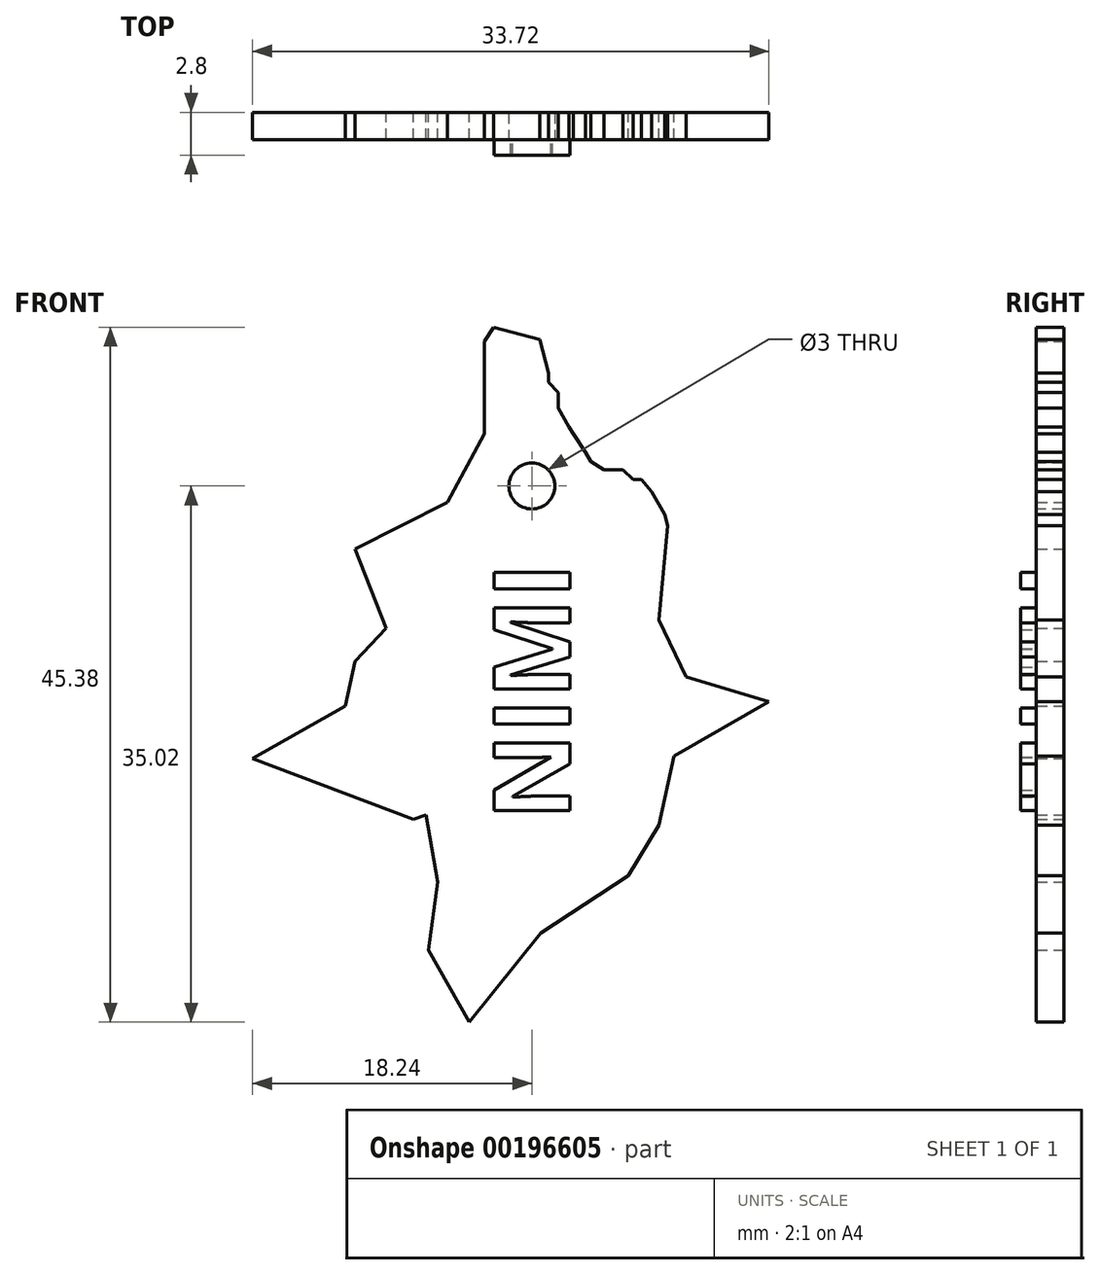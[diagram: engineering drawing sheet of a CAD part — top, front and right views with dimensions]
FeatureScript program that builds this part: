
annotation { "Feature Type Name" : "Feature", "Feature Type Description" : "" }
export const myFeature = defineFeature(function(context is Context, id is Id, definition is map)
    precondition{}
    {
        {
            var Q0;
            Q0=qCreatedBy(makeId("Front.planeOp"),FACE);
            var sketch = newSketch(context, id + "F0", { "sketchPlane" : qUnion([Q0])});
            skLineSegment(sketch, "E0", {"start": v(-3.64, 39.6) * mm, "end": v(1.4, 38.3) * mm});
            skLineSegment(sketch, "E1", {"start": v(1.4, 38.3) * mm, "end": v(2.35, 34.63) * mm});
            skLineSegment(sketch, "E2", {"start": v(2.35, 34.63) * mm, "end": v(2.35, 33.62) * mm});
            skLineSegment(sketch, "E3", {"start": v(2.35, 33.62) * mm, "end": v(3.37, 32.54) * mm});
            skLineSegment(sketch, "E4", {"start": v(3.37, 32.54) * mm, "end": v(3.37, 30.85) * mm});
            skLineSegment(sketch, "E5", {"start": v(3.37, 30.85) * mm, "end": v(4.55, 28.76) * mm});
            skLineSegment(sketch, "E6", {"start": v(4.55, 28.76) * mm, "end": v(5, 28.03) * mm});
            skLineSegment(sketch, "E7", {"start": v(5, 28.03) * mm, "end": v(6.36, 26) * mm});
            skLineSegment(sketch, "E8", {"start": v(6.36, 26) * mm, "end": v(6.92, 25.02) * mm});
            skLineSegment(sketch, "E9", {"start": v(6.92, 25.02) * mm, "end": v(8.34, 24.13) * mm});
            skLineSegment(sketch, "E10", {"start": v(8.34, 24.13) * mm, "end": v(10.43, 24.13) * mm});
            skLineSegment(sketch, "E11", {"start": v(10.43, 24.13) * mm, "end": v(11.56, 23.05) * mm});
            skLineSegment(sketch, "E12", {"start": v(11.56, 23.05) * mm, "end": v(12.46, 23.05) * mm});
            skLineSegment(sketch, "E13", {"start": v(12.46, 23.05) * mm, "end": v(13.56, 21.75) * mm});
            skLineSegment(sketch, "E14", {"start": v(13.56, 21.75) * mm, "end": v(14.32, 20.42) * mm});
            skLineSegment(sketch, "E15", {"start": v(14.32, 20.42) * mm, "end": v(14.98, 19.25) * mm});
            skLineSegment(sketch, "E16", {"start": v(14.98, 19.25) * mm, "end": v(15.3, 18) * mm});
            skLineSegment(sketch, "E17", {"start": v(15.3, 18) * mm, "end": v(14.32, 7.76) * mm});
            skLineSegment(sketch, "E18", {"start": v(14.32, 7.76) * mm, "end": v(17.31, 1.56) * mm});
            skLineSegment(sketch, "E19", {"start": v(17.31, 1.56) * mm, "end": v(26.32, -1.15) * mm});
            skLineSegment(sketch, "E20", {"start": v(26.32, -1.15) * mm, "end": v(15.96, -7.03) * mm});
            skLineSegment(sketch, "E21", {"start": v(15.96, -7.03) * mm, "end": v(14.32, -14.58) * mm});
            skLineSegment(sketch, "E22", {"start": v(14.32, -14.58) * mm, "end": v(11, -20.07) * mm});
            skLineSegment(sketch, "E23", {"start": v(11, -20.07) * mm, "end": v(1.49, -26.31) * mm});
            skLineSegment(sketch, "E24", {"start": v(1.49, -26.31) * mm, "end": v(-6.28, -36.02) * mm});
            skLineSegment(sketch, "E25", {"start": v(-6.28, -36.02) * mm, "end": v(-10.72, -28.18) * mm});
            skLineSegment(sketch, "E26", {"start": v(-10.72, -28.18) * mm, "end": v(-9.75, -20.77) * mm});
            skLineSegment(sketch, "E27", {"start": v(-9.75, -20.77) * mm, "end": v(-11, -13.47) * mm});
            skLineSegment(sketch, "E28", {"start": v(-11, -13.47) * mm, "end": v(-12.4, -13.92) * mm});
            skLineSegment(sketch, "E29", {"start": v(-12.4, -13.92) * mm, "end": v(-29.89, -7.33) * mm});
            skLineSegment(sketch, "E30", {"start": v(-29.89, -7.33) * mm, "end": v(-19.8, -1.6) * mm});
            skLineSegment(sketch, "E31", {"start": v(-19.8, -1.6) * mm, "end": v(-18.74, 3.26) * mm});
            skLineSegment(sketch, "E32", {"start": v(-18.74, 3.26) * mm, "end": v(-15.36, 6.85) * mm});
            skLineSegment(sketch, "E33", {"start": v(-15.36, 6.85) * mm, "end": v(-18.73, 15.49) * mm});
            skLineSegment(sketch, "E34", {"start": v(-18.73, 15.49) * mm, "end": v(-8.7, 20.57) * mm});
            skLineSegment(sketch, "E35", {"start": v(-8.7, 20.57) * mm, "end": v(-4.66, 28.05) * mm});
            skLineSegment(sketch, "E36", {"start": v(-4.66, 28.05) * mm, "end": v(-4.66, 38.08) * mm});
            skLineSegment(sketch, "E37", {"start": v(-4.66, 38.08) * mm, "end": v(-3.64, 39.6) * mm});
            skSolve(sketch);
        }
        {
            var Q0;
            Q0=makeQuery(id+"F0.imprint","IMPRINT",FACE,{"disambiguationData":[TD([[makeQuery(id+"F0.imprint","IMPRINT",EDGE,{"derivedFrom":sQuery(id+"F0.wireOp",EDGE,"E0")}),-1.0]])]});
            extrude(context, id + "F1", {"entities" : qUnion([Q0]), "depth" : 3 * mm});
        }
        {
            var Q0;
            Q0=makeQuery(id+"F1.opExtrude","SWEPT_BODY",BODY,{"disambiguationData":[OSD([sQuery(id+"F0.wireOp",EDGE,"E0"),sQuery(id+"F0.wireOp",EDGE,"E1"),sQuery(id+"F0.wireOp",EDGE,"E2"),sQuery(id+"F0.wireOp",EDGE,"E3"),sQuery(id+"F0.wireOp",EDGE,"E4"),sQuery(id+"F0.wireOp",EDGE,"E5"),sQuery(id+"F0.wireOp",EDGE,"E6"),sQuery(id+"F0.wireOp",EDGE,"E7"),sQuery(id+"F0.wireOp",EDGE,"E8"),sQuery(id+"F0.wireOp",EDGE,"E9"),sQuery(id+"F0.wireOp",EDGE,"E10"),sQuery(id+"F0.wireOp",EDGE,"E11"),sQuery(id+"F0.wireOp",EDGE,"E12"),sQuery(id+"F0.wireOp",EDGE,"E13"),sQuery(id+"F0.wireOp",EDGE,"E14"),sQuery(id+"F0.wireOp",EDGE,"E15"),sQuery(id+"F0.wireOp",EDGE,"E16"),sQuery(id+"F0.wireOp",EDGE,"E17"),sQuery(id+"F0.wireOp",EDGE,"E18"),sQuery(id+"F0.wireOp",EDGE,"E19"),sQuery(id+"F0.wireOp",EDGE,"E20"),sQuery(id+"F0.wireOp",EDGE,"E21"),sQuery(id+"F0.wireOp",EDGE,"E22"),sQuery(id+"F0.wireOp",EDGE,"E23"),sQuery(id+"F0.wireOp",EDGE,"E24"),sQuery(id+"F0.wireOp",EDGE,"E25"),sQuery(id+"F0.wireOp",EDGE,"E26"),sQuery(id+"F0.wireOp",EDGE,"E27"),sQuery(id+"F0.wireOp",EDGE,"E28"),sQuery(id+"F0.wireOp",EDGE,"E29"),sQuery(id+"F0.wireOp",EDGE,"E30"),sQuery(id+"F0.wireOp",EDGE,"E31"),sQuery(id+"F0.wireOp",EDGE,"E32"),sQuery(id+"F0.wireOp",EDGE,"E33"),sQuery(id+"F0.wireOp",EDGE,"E34"),sQuery(id+"F0.wireOp",EDGE,"E35"),sQuery(id+"F0.wireOp",EDGE,"E36"),sQuery(id+"F0.wireOp",EDGE,"E37")])]});
            var Q1;
            Q1=makeQuery(id+"F1.opExtrude","CAP_VERTEX",VERTEX,{"disambiguationData":[OSD([sQuery(id+"F0.wireOp",EDGE,"E24"),sQuery(id+"F0.wireOp",EDGE,"E25")])],"isStart":false});
            transform(context, id + "F2", {"entities" : qUnion([Q0]), "transformType" : TransformType.SCALE_UNIFORMLY, "scale" : 0.6, "scalePoint" : qUnion([Q1]), "makeCopy" : false});
        }
        {
            var Q0;
            Q0=makeQuery(id+"F1.opExtrude","CAP_FACE",FACE,{"disambiguationData":[OSD([sQuery(id+"F0.wireOp",EDGE,"E0"),sQuery(id+"F0.wireOp",EDGE,"E1"),sQuery(id+"F0.wireOp",EDGE,"E2"),sQuery(id+"F0.wireOp",EDGE,"E3"),sQuery(id+"F0.wireOp",EDGE,"E4"),sQuery(id+"F0.wireOp",EDGE,"E5"),sQuery(id+"F0.wireOp",EDGE,"E6"),sQuery(id+"F0.wireOp",EDGE,"E7"),sQuery(id+"F0.wireOp",EDGE,"E8"),sQuery(id+"F0.wireOp",EDGE,"E9"),sQuery(id+"F0.wireOp",EDGE,"E10"),sQuery(id+"F0.wireOp",EDGE,"E11"),sQuery(id+"F0.wireOp",EDGE,"E12"),sQuery(id+"F0.wireOp",EDGE,"E13"),sQuery(id+"F0.wireOp",EDGE,"E14"),sQuery(id+"F0.wireOp",EDGE,"E15"),sQuery(id+"F0.wireOp",EDGE,"E16"),sQuery(id+"F0.wireOp",EDGE,"E17"),sQuery(id+"F0.wireOp",EDGE,"E18"),sQuery(id+"F0.wireOp",EDGE,"E19"),sQuery(id+"F0.wireOp",EDGE,"E20"),sQuery(id+"F0.wireOp",EDGE,"E21"),sQuery(id+"F0.wireOp",EDGE,"E22"),sQuery(id+"F0.wireOp",EDGE,"E23"),sQuery(id+"F0.wireOp",EDGE,"E24"),sQuery(id+"F0.wireOp",EDGE,"E25"),sQuery(id+"F0.wireOp",EDGE,"E26"),sQuery(id+"F0.wireOp",EDGE,"E27"),sQuery(id+"F0.wireOp",EDGE,"E28"),sQuery(id+"F0.wireOp",EDGE,"E29"),sQuery(id+"F0.wireOp",EDGE,"E30"),sQuery(id+"F0.wireOp",EDGE,"E31"),sQuery(id+"F0.wireOp",EDGE,"E32"),sQuery(id+"F0.wireOp",EDGE,"E33"),sQuery(id+"F0.wireOp",EDGE,"E34"),sQuery(id+"F0.wireOp",EDGE,"E35"),sQuery(id+"F0.wireOp",EDGE,"E36"),sQuery(id+"F0.wireOp",EDGE,"E37")])],"isStart":false});
            var sketch = newSketch(context, id + "F3", { "sketchPlane" : qUnion([Q0])});
            skCircle(sketch, "E38", {"center": v(-2.2, -1) * mm, "radius": 1.5 * mm});
            skSolve(sketch);
        }
        {
            var Q0;
            Q0=qSketchRegion(id+"F3",true);
            extrude(context, id + "F4", {"entities" : qUnion([Q0]), "operationType" : NewBodyOperationType.REMOVE, "oppositeDirection" : true, "depth" : 25 * mm});
        }
        {
            var Q0;
            Q0=makeQuery(id+"F1.opExtrude","CAP_FACE",FACE,{"disambiguationData":[OSD([sQuery(id+"F0.wireOp",EDGE,"E0"),sQuery(id+"F0.wireOp",EDGE,"E1"),sQuery(id+"F0.wireOp",EDGE,"E2"),sQuery(id+"F0.wireOp",EDGE,"E3"),sQuery(id+"F0.wireOp",EDGE,"E4"),sQuery(id+"F0.wireOp",EDGE,"E5"),sQuery(id+"F0.wireOp",EDGE,"E6"),sQuery(id+"F0.wireOp",EDGE,"E7"),sQuery(id+"F0.wireOp",EDGE,"E8"),sQuery(id+"F0.wireOp",EDGE,"E9"),sQuery(id+"F0.wireOp",EDGE,"E10"),sQuery(id+"F0.wireOp",EDGE,"E11"),sQuery(id+"F0.wireOp",EDGE,"E12"),sQuery(id+"F0.wireOp",EDGE,"E13"),sQuery(id+"F0.wireOp",EDGE,"E14"),sQuery(id+"F0.wireOp",EDGE,"E15"),sQuery(id+"F0.wireOp",EDGE,"E16"),sQuery(id+"F0.wireOp",EDGE,"E17"),sQuery(id+"F0.wireOp",EDGE,"E18"),sQuery(id+"F0.wireOp",EDGE,"E19"),sQuery(id+"F0.wireOp",EDGE,"E20"),sQuery(id+"F0.wireOp",EDGE,"E21"),sQuery(id+"F0.wireOp",EDGE,"E22"),sQuery(id+"F0.wireOp",EDGE,"E23"),sQuery(id+"F0.wireOp",EDGE,"E24"),sQuery(id+"F0.wireOp",EDGE,"E25"),sQuery(id+"F0.wireOp",EDGE,"E26"),sQuery(id+"F0.wireOp",EDGE,"E27"),sQuery(id+"F0.wireOp",EDGE,"E28"),sQuery(id+"F0.wireOp",EDGE,"E29"),sQuery(id+"F0.wireOp",EDGE,"E30"),sQuery(id+"F0.wireOp",EDGE,"E31"),sQuery(id+"F0.wireOp",EDGE,"E32"),sQuery(id+"F0.wireOp",EDGE,"E33"),sQuery(id+"F0.wireOp",EDGE,"E34"),sQuery(id+"F0.wireOp",EDGE,"E35"),sQuery(id+"F0.wireOp",EDGE,"E36"),sQuery(id+"F0.wireOp",EDGE,"E37")])],"isStart":false});
            var sketch = newSketch(context, id + "F5", { "sketchPlane" : qUnion([Q0])});
            skText(sketch, "E39", { "text": "NIMI", "fontName": "OpenSans-Bold.ttf"});
            skLineSegment(sketch, "E40", {"start": v(-2.2, -6.2) * mm, "end": v(-2.2, -1) * mm, "construction": true});
            const initialGuessF5  = {"E39": [0.0003, -0.02282, 0, 1, 0.005]};
            skSetInitialGuess(sketch, initialGuessF5);
            skSolve(sketch);
        }
        {
            var Q0;
            Q0 = qSketchRegion(id + "F5", true);
            extrude(context, id + "F6", {"entities" : qUnion([Q0]), "operationType" : NewBodyOperationType.ADD, "depth" : 1 * mm});
        }
    });
